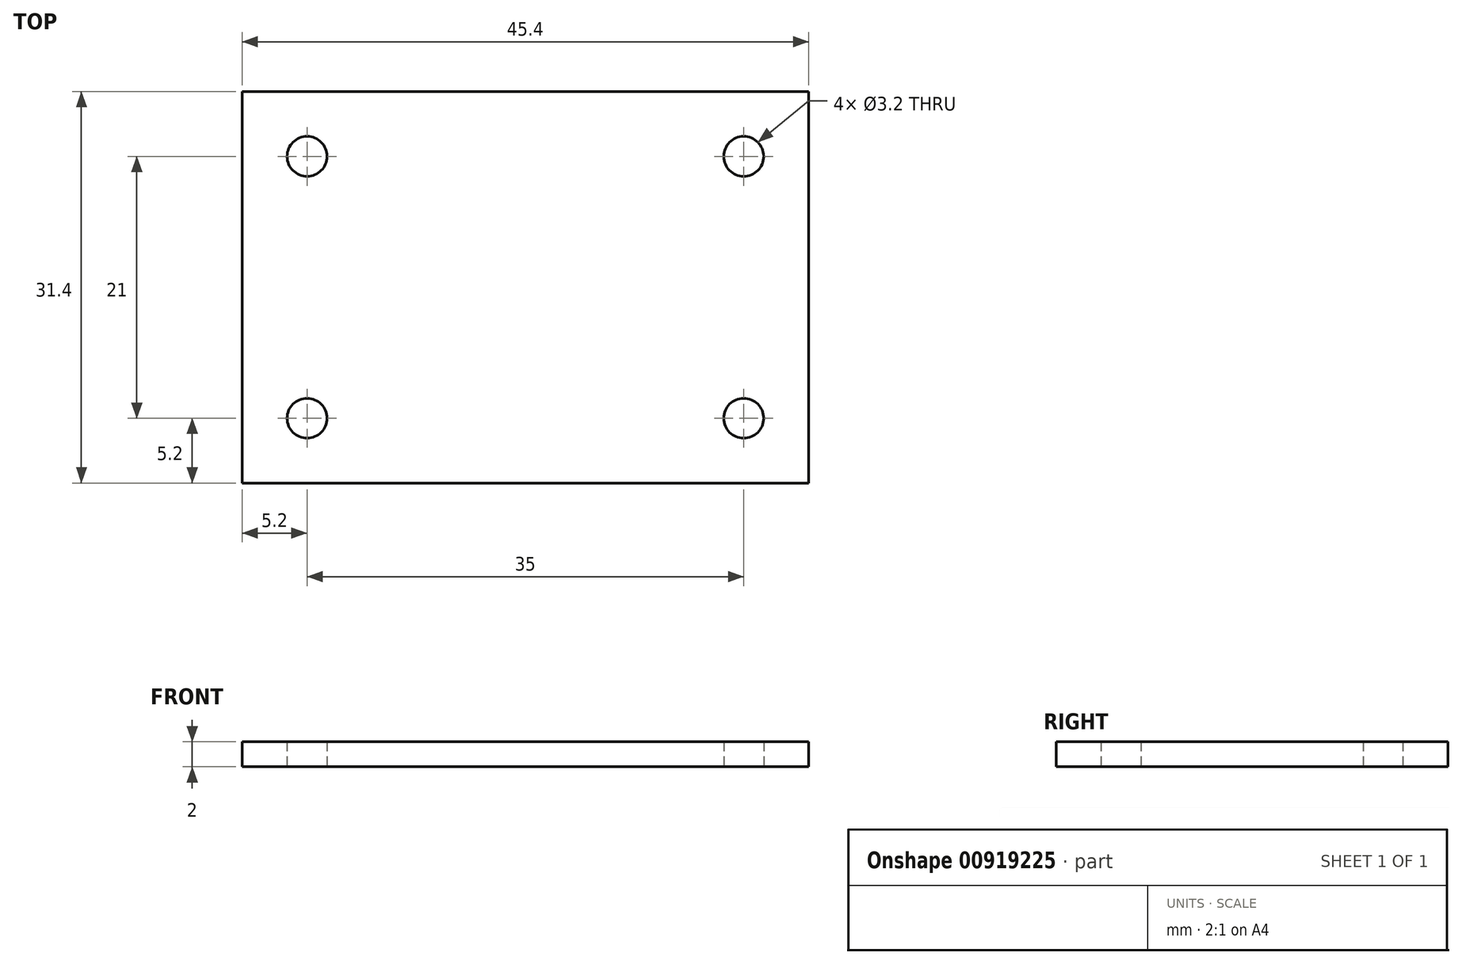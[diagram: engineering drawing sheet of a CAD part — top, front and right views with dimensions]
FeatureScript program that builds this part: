
annotation { "Feature Type Name" : "Feature", "Feature Type Description" : "" }
export const myFeature = defineFeature(function(context is Context, id is Id, definition is map)
    precondition{}
    {
        {
            assignVariable(context, id + "F0", {"name" : "thickness", "anyValue" : 2});
        }
        {
            var Q0;
            Q0=qCreatedBy(makeId("Top.planeOp"),FACE);
            var sketch = newSketch(context, id + "F1", { "sketchPlane" : qUnion([Q0])});
            skCircle(sketch, "E0", {"center": v(-18, 10.5) * mm, "radius": 1.6 * mm});
            skCircle(sketch, "E1", {"center": v(17, 10.5) * mm, "radius": 1.6 * mm});
            skCircle(sketch, "E2", {"center": v(17, -10.5) * mm, "radius": 1.6 * mm});
            skCircle(sketch, "E3", {"center": v(-18, -10.5) * mm, "radius": 1.6 * mm});
            skLineSegment(sketch, "E4.left", {"start": v(-23.2, 15.7) * mm, "end": v(-23.2, -15.7) * mm});
            skLineSegment(sketch, "E4.right", {"start": v(22.2, 15.7) * mm, "end": v(22.2, -15.7) * mm});
            skLineSegment(sketch, "E5", {"start": v(-23.2, 15.7) * mm, "end": v(22.2, 15.7) * mm});
            skLineSegment(sketch, "E6", {"start": v(22.2, -15.7) * mm, "end": v(-23.2, -15.7) * mm});
            skSolve(sketch);
        }
        {
            var Q0;
            Q0=makeQuery(id+"F1.imprint","IMPRINT",FACE,{"disambiguationData":[TD([[makeQuery(id+"F1.imprint","IMPRINT",EDGE,{"derivedFrom":sQuery(id+"F1.wireOp",EDGE,"E0")}),-1.0]])]});
            extrude(context, id + "F2", {"entities" : qUnion([Q0]), "depth" : (getVariable(context, 'thickness')) * mm, "offsetDistance" : 25 * mm});
        }
    });
